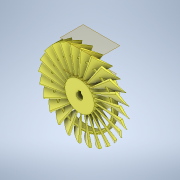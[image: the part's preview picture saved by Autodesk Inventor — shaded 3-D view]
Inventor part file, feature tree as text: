
AUTODESK INVENTOR PART (.ipt)
format: ipt  version: 2021.2 (Build 252289000, 289)  size: 3,176,960 bytes
history: native  units: in
note: dims shown in document units (in); Inventor stores cm internally (conversion verified against a paired STEP export)
features: sketch x6, extrude x4, plane x2, loft x1, pattern_circular x1, revolve x1, other x1
ambient origin geometry x8: Origin, YZ Plane, XZ Plane, XY Plane, X Axis, Y Axis, Z Axis, Center Point
bodies: Solid1 (feature_tree)
feature tree (16):
  extrude  "Extrusion1"  Depth=1.0in
  plane  "Work Plane1"
  plane  "Work Plane2"
  extrude  "Extrusion4"  Depth=2.0in
  loft  "Loft2"
  pattern_circular  "Circular Pattern5"  Count=24 Angle=360.0deg
  extrude  "Extrusion5"  Depth=0.125in
  revolve  "Revolution4"  [1 undecoded]
  extrude  "Extrusion6"  TaperAngle=0.0deg  [1 undecoded]
  sketch  "Sketch1"  dims[d0=1.4in d1=1.0in d2=0.0777in]
  sketch  "Sketch5"  dims[d4=0.75in d15=2.0in]
  sketch  "Sketch6"  dims[d28=0.0312in d29=0.5in d30=0.0in]
  other  "Edges2"
  sketch  "Sketch8"  dims[d31=0.0in d32=90.0deg]
  sketch  "Sketch12"  dims[d33=0.0in d34=90.0deg d35=9.4488in d36=360.0deg]
  sketch  "Sketch13"  dims[d39=0.315in d40=0.125in d41=0.125in d42=0.0in d43=0.0in d60=0.125in d61=0.3in d62=0.05in d63=0.5in d64=0.6in d65=90.0deg d66=3.9375in d67=0.0in d68=0.0in]
note: 2 required parameter values undecoded (feature->parameter linkage not recoverable at this tier; creation-order binding heuristic only, values carry confidence <= 0.55)